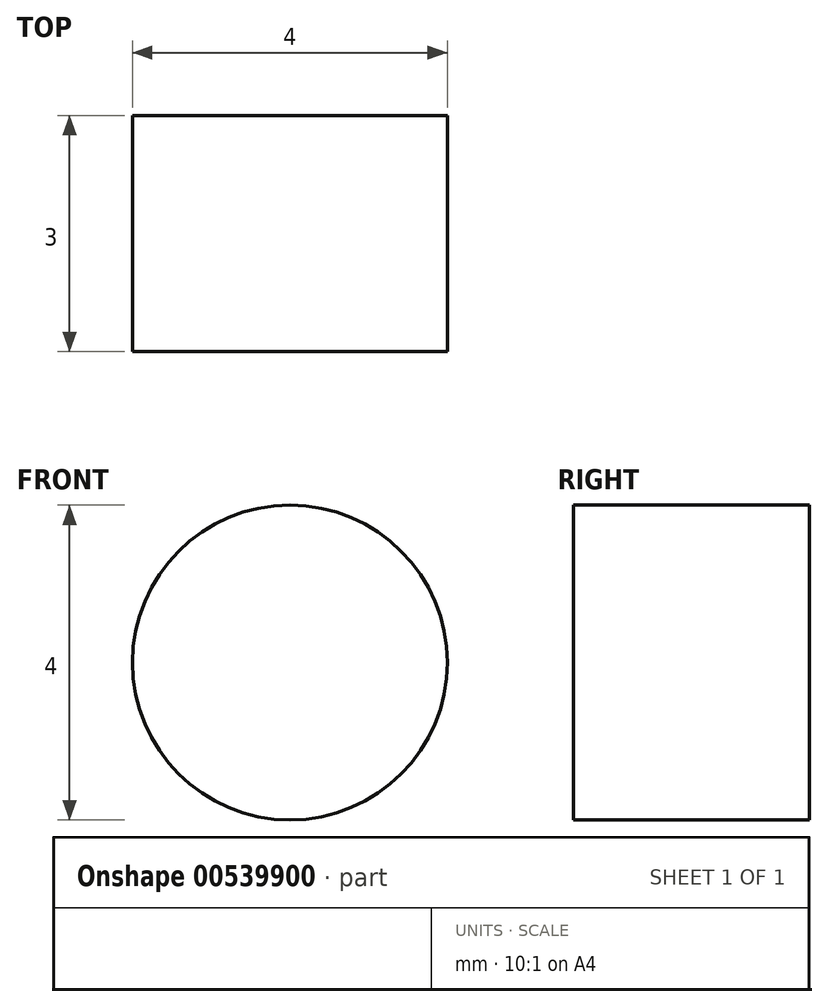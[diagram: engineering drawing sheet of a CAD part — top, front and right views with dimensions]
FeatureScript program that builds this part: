
annotation { "Feature Type Name" : "Feature", "Feature Type Description" : "" }
export const myFeature = defineFeature(function(context is Context, id is Id, definition is map)
    precondition{}
    {
        {
            var Q0;
            Q0=qCreatedBy(makeId("Top.planeOp"),FACE);
            var sketch = newSketch(context, id + "F0", { "sketchPlane" : qUnion([Q0])});
            skArc(sketch, "E0", {"start": v(0, 24) * mm, "mid": v(-24, 0) * mm, "end": v(0, -24) * mm});
            skArc(sketch, "E1", {"start": v(-21.73, 16.03) * mm, "mid": v(-27, 0.56) * mm, "end": v(-22.37, -15.12) * mm});
            skLineSegment(sketch, "E2", {"start": v(-20, 0) * mm, "end": v(-20, -29.41) * mm, "construction": true});
            skLineSegment(sketch, "E3", {"start": v(0, -28) * mm, "end": v(-30.93, -28) * mm, "construction": true});
            skCircle(sketch, "E4", {"center": v(-20, -28) * mm, "radius": 1.5 * mm});
            skArc(sketch, "E5", {"start": v(-23.3, -26.2) * mm, "mid": v(-20, -31.75) * mm, "end": v(-16.7, -26.2) * mm});
            skPoint(sketch, "E6.0.internal.snap0", {"position": v(-20, -14.7) * mm});
            skFitSpline(sketch, "E6", {"points": [v(-20, -13.27) * mm, v(-16.7, -26.2) * mm], "startDerivative": vector(6.66, -10.04) * mm, "endDerivative": vector(5.78, -10.57) * mm});
            skLineSegment(sketch, "E7", {"start": v(-16.7, -26.2) * mm, "end": v(-33.32, -26.2) * mm, "construction": true});
            skFitSpline(sketch, "E8", {"points": [v(-22.37, -15.12) * mm, v(-23.3, -26.2) * mm], "startDerivative": vector(2.28, -3.37) * mm, "endDerivative": vector(-7.2, -13.19) * mm});
            skLineSegment(sketch, "E9", {"start": v(0, -24) * mm, "end": v(0, -27) * mm});
            skArc(sketch, "E10.MirrorCS", {"start": v(0, 24) * mm, "mid": v(24, 0) * mm, "end": v(0, -24) * mm});
            skArc(sketch, "E11.MirrorCS", {"start": v(21.73, 16.03) * mm, "mid": v(27, 0.56) * mm, "end": v(22.37, -15.12) * mm});
            skFitSpline(sketch, "E12.MirrorCS", {"points": [v(22.37, -15.12) * mm, v(23.3, -26.2) * mm], "startDerivative": vector(-2.28, -3.37) * mm, "endDerivative": vector(7.2, -13.19) * mm});
            skFitSpline(sketch, "E13.MirrorCS", {"points": [v(20, -13.27) * mm, v(16.7, -26.2) * mm], "startDerivative": vector(-6.66, -10.04) * mm, "endDerivative": vector(-5.78, -10.57) * mm});
            skArc(sketch, "E14.MirrorCS", {"start": v(23.3, -26.2) * mm, "mid": v(20, -31.75) * mm, "end": v(16.7, -26.2) * mm});
            skLineSegment(sketch, "E15.bottom", {"start": v(0, 27) * mm, "end": v(50, 27) * mm});
            skLineSegment(sketch, "E15.top", {"start": v(25.75, 24) * mm, "end": v(50, 24) * mm});
            skLineSegment(sketch, "E15.right", {"start": v(50, 27) * mm, "end": v(50, 24) * mm});
            skLineSegment(sketch, "E16.MirrorCS", {"start": v(-25.75, 24) * mm, "end": v(-50, 24) * mm});
            skLineSegment(sketch, "E17.MirrorCS", {"start": v(0, 27) * mm, "end": v(-50, 27) * mm});
            skLineSegment(sketch, "E18.MirrorCS", {"start": v(-50, 27) * mm, "end": v(-50, 24) * mm});
            skPoint(sketch, "E19.orphan", {"position": v(0, 24) * mm});
            skPoint(sketch, "E20.orphan", {"position": v(0, 27) * mm});
            skPoint(sketch, "E21.visualSharp", {"position": v(-12.37, 24) * mm});
            skArc(sketch, "E21.filletArc", {"start": v(-21.73, 16.03) * mm, "mid": v(-21.29, 21.25) * mm, "end": v(-25.75, 24) * mm});
            skPoint(sketch, "E22.visualSharp", {"position": v(12.37, 24) * mm});
            skArc(sketch, "E22.filletArc", {"start": v(25.75, 24) * mm, "mid": v(21.29, 21.25) * mm, "end": v(21.73, 16.03) * mm});
            skSolve(sketch);
        }
        {
            var Q0;
            Q0=makeQuery(id+"F0.imprint","IMPRINT",FACE,{"disambiguationData":[TD([[makeQuery(id+"F0.imprint","IMPRINT",EDGE,{"derivedFrom":sQuery(id+"F0.wireOp",EDGE,"E1")}),1.0]])]});
            extrude(context, id + "F1", {"entities" : qUnion([Q0]), "depth" : 80 * mm, "offsetDistance" : 25 * mm});
        }
        {
            var Q0;
            Q0=makeQuery(id+"F1.opExtrude","CAP_FACE",FACE,{"disambiguationData":[OSD([sQuery(id+"F0.wireOp",EDGE,"E0"),sQuery(id+"F0.wireOp",EDGE,"E1"),sQuery(id+"F0.wireOp",EDGE,"E4"),sQuery(id+"F0.wireOp",EDGE,"E5"),sQuery(id+"F0.wireOp",EDGE,"E6"),sQuery(id+"F0.wireOp",EDGE,"E8"),sQuery(id+"F0.wireOp",EDGE,"E10.MirrorCS"),sQuery(id+"F0.wireOp",EDGE,"E11.MirrorCS"),sQuery(id+"F0.wireOp",EDGE,"E12.MirrorCS"),sQuery(id+"F0.wireOp",EDGE,"E13.MirrorCS"),sQuery(id+"F0.wireOp",EDGE,"E14.MirrorCS"),sQuery(id+"F0.wireOp",EDGE,"E15.bottom"),sQuery(id+"F0.wireOp",EDGE,"E15.top"),sQuery(id+"F0.wireOp",EDGE,"E15.right"),sQuery(id+"F0.wireOp",EDGE,"E16.MirrorCS"),sQuery(id+"F0.wireOp",EDGE,"E17.MirrorCS"),sQuery(id+"F0.wireOp",EDGE,"E18.MirrorCS"),sQuery(id+"F0.wireOp",EDGE,"E21.filletArc"),sQuery(id+"F0.wireOp",EDGE,"E22.filletArc")])],"isStart":false});
            var sketch = newSketch(context, id + "F2", { "sketchPlane" : qUnion([Q0])});
            skLineSegment(sketch, "E23.bottom", {"start": v(-50, 27) * mm, "end": v(50, 27) * mm});
            skLineSegment(sketch, "E23.top", {"start": v(-50, 24) * mm, "end": v(50, 24) * mm});
            skLineSegment(sketch, "E23.left", {"start": v(-50, 27) * mm, "end": v(-50, 24) * mm});
            skLineSegment(sketch, "E23.right", {"start": v(50, 27) * mm, "end": v(50, 24) * mm});
            skSolve(sketch);
        }
        {
            var Q0;
            Q0=makeQuery(id+"F2.imprint","IMPRINT",FACE,{"disambiguationData":[TD([[makeQuery(id+"F2.imprint","IMPRINT",EDGE,{"derivedFrom":sQuery(id+"F2.wireOp",EDGE,"E23.bottom")}),-1.0]])]});
            extrude(context, id + "F3", {"entities" : qUnion([Q0]), "operationType" : NewBodyOperationType.ADD, "depth" : 10 * mm, "offsetDistance" : 25 * mm});
        }
        {
            var Q0;
            Q0=makeQuery(id+"F1.opExtrude","CAP_FACE",FACE,{"disambiguationData":[OSD([sQuery(id+"F0.wireOp",EDGE,"E0"),sQuery(id+"F0.wireOp",EDGE,"E1"),sQuery(id+"F0.wireOp",EDGE,"E4"),sQuery(id+"F0.wireOp",EDGE,"E5"),sQuery(id+"F0.wireOp",EDGE,"E6"),sQuery(id+"F0.wireOp",EDGE,"E8"),sQuery(id+"F0.wireOp",EDGE,"E10.MirrorCS"),sQuery(id+"F0.wireOp",EDGE,"E11.MirrorCS"),sQuery(id+"F0.wireOp",EDGE,"E12.MirrorCS"),sQuery(id+"F0.wireOp",EDGE,"E13.MirrorCS"),sQuery(id+"F0.wireOp",EDGE,"E14.MirrorCS"),sQuery(id+"F0.wireOp",EDGE,"E15.bottom"),sQuery(id+"F0.wireOp",EDGE,"E15.top"),sQuery(id+"F0.wireOp",EDGE,"E15.right"),sQuery(id+"F0.wireOp",EDGE,"E16.MirrorCS"),sQuery(id+"F0.wireOp",EDGE,"E17.MirrorCS"),sQuery(id+"F0.wireOp",EDGE,"E18.MirrorCS"),sQuery(id+"F0.wireOp",EDGE,"E21.filletArc"),sQuery(id+"F0.wireOp",EDGE,"E22.filletArc")])],"isStart":true});
            var sketch = newSketch(context, id + "F4", { "sketchPlane" : qUnion([Q0])});
            skLineSegment(sketch, "E24.bottom", {"start": v(50, -27) * mm, "end": v(-50, -27) * mm});
            skLineSegment(sketch, "E24.top", {"start": v(50, -24) * mm, "end": v(-50, -24) * mm});
            skLineSegment(sketch, "E24.left", {"start": v(50, -27) * mm, "end": v(50, -24) * mm});
            skLineSegment(sketch, "E24.right", {"start": v(-50, -27) * mm, "end": v(-50, -24) * mm});
            skSolve(sketch);
        }
        {
            var Q0;
            Q0=makeQuery(id+"F4.imprint","IMPRINT",FACE,{"disambiguationData":[TD([[makeQuery(id+"F4.imprint","IMPRINT",EDGE,{"derivedFrom":sQuery(id+"F4.wireOp",EDGE,"E24.bottom")}),1.0]])]});
            extrude(context, id + "F5", {"entities" : qUnion([Q0]), "operationType" : NewBodyOperationType.ADD, "depth" : 10 * mm, "offsetDistance" : 25 * mm});
        }
        {
            var Q0;
            Q0=qCreatedBy(makeId("Right.planeOp"),FACE);
            var sketch = newSketch(context, id + "F6", { "sketchPlane" : qUnion([Q0])});
            skPoint(sketch, "E25.endSnap0", {"position": v(24, 40) * mm});
            skLineSegment(sketch, "E26.top", {"start": v(24, 60) * mm, "end": v(-33.46, 60) * mm});
            skLineSegment(sketch, "E26.left", {"start": v(24, 40) * mm, "end": v(24, 60) * mm});
            skLineSegment(sketch, "E26.right", {"start": v(-33.46, 40) * mm, "end": v(-33.46, 60) * mm});
            skLineSegment(sketch, "E27.MirrorCS", {"start": v(24, 20) * mm, "end": v(-33.46, 20) * mm});
            skLineSegment(sketch, "E28.MirrorCS", {"start": v(24, 40) * mm, "end": v(24, 20) * mm});
            skLineSegment(sketch, "E29.MirrorCS", {"start": v(-33.46, 40) * mm, "end": v(-33.46, 20) * mm});
            skSolve(sketch);
        }
        {
            var Q0;
            Q0 = qSketchRegion(id + "F6", true);
            extrude(context, id + "F7", {"entities" : qUnion([Q0]), "operationType" : NewBodyOperationType.REMOVE, "endBound" : BoundingType.THROUGH_ALL, "oppositeDirection" : true, "depth" : 25 * mm, "offsetDistance" : 25 * mm, "hasSecondDirection" : true, "secondDirectionBound" : SecondDirectionBoundingType.THROUGH_ALL, "secondDirectionOppositeDirection" : false, "secondDirectionDepth" : 25 * mm});
        }
        {
            var Q0;
            {var subQ1=sQuery(id+"F2.wireOp",EDGE,"E23.top");var subQ5=sQuery(id+"F0.wireOp",EDGE,"E21.filletArc");Q0=makeQuery(id+"F3.boolean.opBoolean","SPLIT",EDGE,{"disambiguationData":[TD([makeQuery(id+"F1.opExtrude","SWEPT_FACE",FACE,{"disambiguationData":[OSD([subQ5])]})])],"derivedFrom":makeQuery(id+"F3.opExtrude","CAP_EDGE",EDGE,{"disambiguationData":[OSD([subQ1])],"isStart":true})});}
            var Q1;
            {var subQ0=sQuery(id+"F6.wireOp",EDGE,"E28.MirrorCS");var subQ1=sQuery(id+"F6.wireOp",EDGE,"E27.MirrorCS");Q1=makeQuery(id+"F7.boolean.opBoolean","COPY",EDGE,{"disambiguationData":[TD([makeQuery(id+"F1.opExtrude","SWEPT_FACE",FACE,{"disambiguationData":[OSD([sQuery(id+"F0.wireOp",EDGE,"E21.filletArc")])]})])],"derivedFrom":makeQuery(id+"F7.opExtrude","SWEPT_EDGE",EDGE,{"disambiguationData":[OSD([subQ1,subQ0])]})});}
            var Q2;
            {var subQ0=sQuery(id+"F6.wireOp",EDGE,"E26.top");var subQ1=sQuery(id+"F6.wireOp",EDGE,"E26.left");Q2=makeQuery(id+"F7.boolean.opBoolean","COPY",EDGE,{"disambiguationData":[TD([makeQuery(id+"F1.opExtrude","SWEPT_FACE",FACE,{"disambiguationData":[OSD([sQuery(id+"F0.wireOp",EDGE,"E22.filletArc")])]})])],"derivedFrom":makeQuery(id+"F7.opExtrude","SWEPT_EDGE",EDGE,{"disambiguationData":[OSD([subQ0,subQ1])]})});}
            var Q3;
            {var subQ4=sQuery(id+"F0.wireOp",EDGE,"E22.filletArc");var subQ5=sQuery(id+"F4.wireOp",EDGE,"E24.top");Q3=makeQuery(id+"F5.boolean.opBoolean","SPLIT",EDGE,{"disambiguationData":[TD([makeQuery(id+"F1.opExtrude","SWEPT_FACE",FACE,{"disambiguationData":[OSD([subQ4])]})])],"derivedFrom":makeQuery(id+"F5.opExtrude","CAP_EDGE",EDGE,{"disambiguationData":[OSD([subQ5])],"isStart":true})});}
            fillet(context, id + "F8", {"entities" : qUnion([Q0, Q1, Q2, Q3]), "radius" : 2 * mm, "tangentPropagation" : true, "allowEdgeOverflow" : false});
        }
        {
            var Q0;
            Q0=makeQuery(id+"F5.boolean.opBoolean","MERGE",FACE,{"derivedFrom":[makeQuery(id+"F3.boolean.opBoolean","MERGE",FACE,{"derivedFrom":[makeQuery(id+"F1.opExtrude","SWEPT_FACE",FACE,{"disambiguationData":[OSD([sQuery(id+"F0.wireOp",EDGE,"E15.bottom"),sQuery(id+"F0.wireOp",EDGE,"E17.MirrorCS")])]}),makeQuery(id+"F3.opExtrude","SWEPT_FACE",FACE,{"disambiguationData":[OSD([sQuery(id+"F2.wireOp",EDGE,"E23.bottom")])]})]}),makeQuery(id+"F5.opExtrude","SWEPT_FACE",FACE,{"disambiguationData":[OSD([sQuery(id+"F4.wireOp",EDGE,"E24.bottom")])]})]});
            var sketch = newSketch(context, id + "F9", { "sketchPlane" : qUnion([Q0])});
            skLineSegment(sketch, "E30", {"start": v(-50, 40) * mm, "end": v(51.9, 40) * mm, "construction": true});
            skCircle(sketch, "E31", {"center": v(-42.5, 40) * mm, "radius": 2 * mm});
            skCircle(sketch, "E32.MirrorC", {"center": v(42.5, 40) * mm, "radius": 2 * mm});
            skSolve(sketch);
        }
        {
            var Q0;
            Q0=makeQuery(id+"F9.imprint","IMPRINT",FACE,{"disambiguationData":[TD([[makeQuery(id+"F9.imprint","IMPRINT",EDGE,{"derivedFrom":sQuery(id+"F9.wireOp",EDGE,"E32.MirrorC")}),-1.0]])]});
            var Q1;
            Q1=makeQuery(id+"F9.imprint","IMPRINT",FACE,{"disambiguationData":[TD([[makeQuery(id+"F9.imprint","IMPRINT",EDGE,{"derivedFrom":sQuery(id+"F9.wireOp",EDGE,"E31")}),1.0]])]});
            extrude(context, id + "F10", {"entities" : qUnion([Q0, Q1]), "operationType" : NewBodyOperationType.REMOVE, "endBound" : BoundingType.THROUGH_ALL, "oppositeDirection" : true, "depth" : 25 * mm, "offsetDistance" : 25 * mm});
        }
    });
